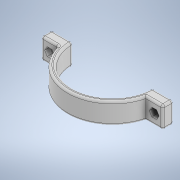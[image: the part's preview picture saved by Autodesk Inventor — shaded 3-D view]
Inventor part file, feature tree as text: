
AUTODESK INVENTOR PART (.ipt)
format: ipt  version: 2020 (Build 240168000, 168)  size: 235,520 bytes
history: native  units: in
note: dims shown in document units (in); Inventor stores cm internally (conversion verified against a paired STEP export)
features: sketch x5, extrude x4, mirror x2, shell x1, plane x1, hole x1, fillet x1
ambient origin geometry x8: Origin, YZ Plane, XZ Plane, XY Plane, X Axis, Y Axis, Z Axis, Center Point
bodies: Solid1 (feature_tree)
feature tree (15):
  extrude  "Extrusion1"  Depth=0.7874in TaperAngle=0.0deg
  shell  "Shell1"  Thickness=0.1969in
  extrude  "Extrusion2"  [1 undecoded]
  plane  "Work Plane1"
  extrude  "Extrusion3"  Depth=0.3937in
  mirror  "Mirror1"
  extrude  "Extrusion4"  Depth=0.0787in
  hole  "Hole3"  [1 undecoded]
  mirror  "Mirror3"
  fillet  "Fillet1"  [1 undecoded]
  sketch  "Sketch1"  dims[d0=3.3465in d1=0.7874in d2=0.0in d3=0.1969in]
  sketch  "Sketch2"  dims[d4=0.3937in d5=0.0in d6=-1.6732in]
  sketch  "Sketch3"  dims[d7=0.7874in d8=0.3937in]
  sketch  "Sketch6"  dims[d9=0.0787in d10=0.5906in d11=0.0in d12=0.0in d27=0.315in]
  sketch  "Sketch7"  dims[d28=0.1969in d29=0.0in d30=0.2165in d31=0.2362in d32=0.4819in d33=0.1409in d34=0.5635in d35=0.315in d36=0.8108in d37=0.0787in]
note: 3 required parameter values undecoded (feature->parameter linkage not recoverable at this tier; creation-order binding heuristic only, values carry confidence <= 0.55)
